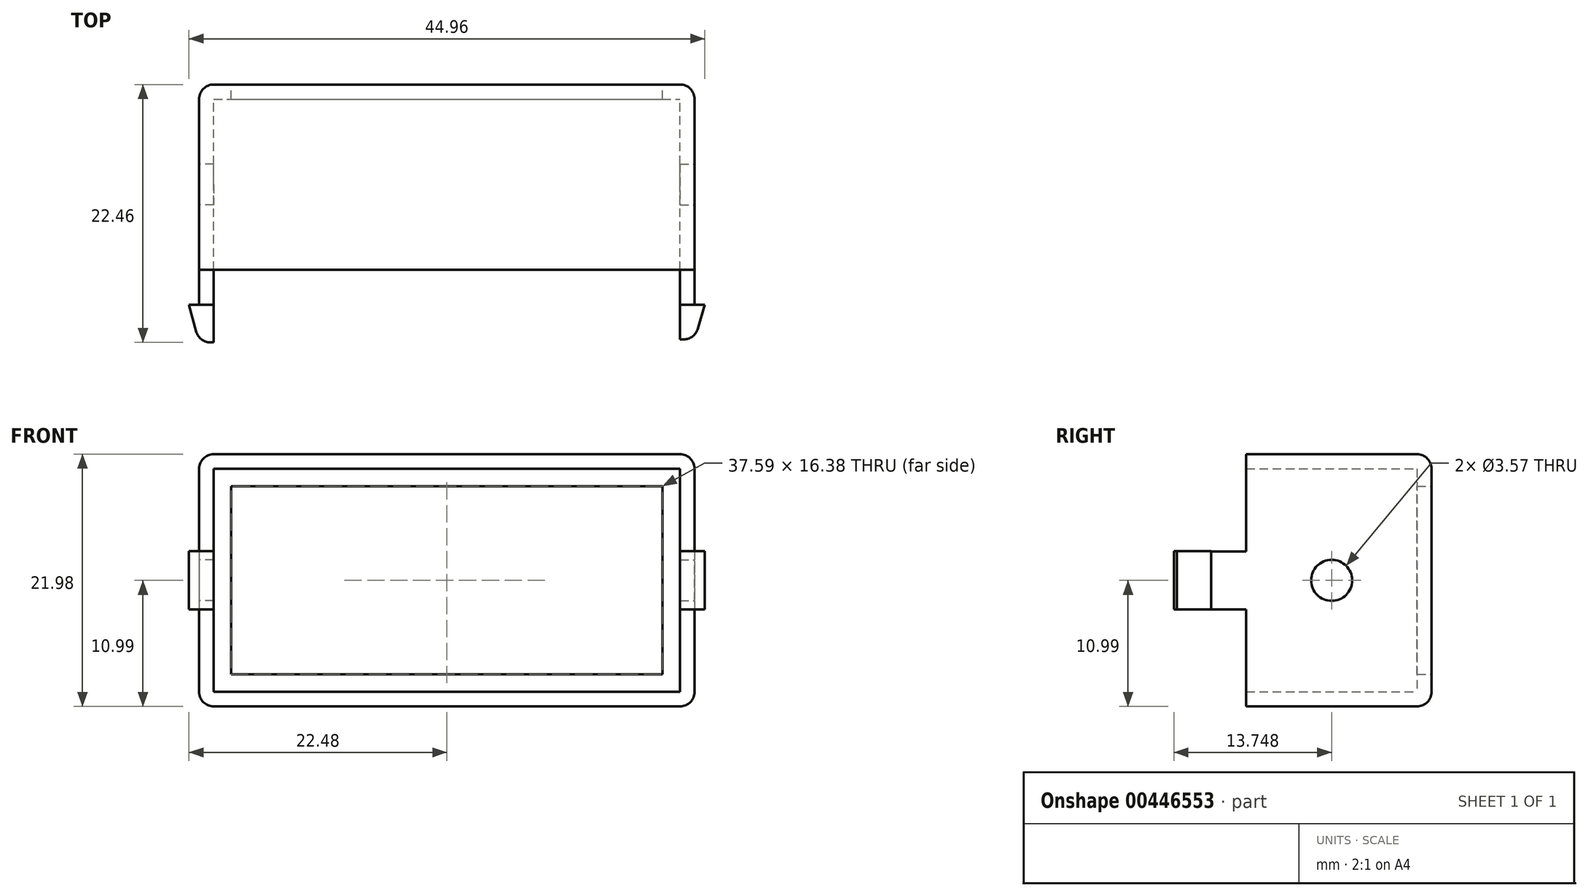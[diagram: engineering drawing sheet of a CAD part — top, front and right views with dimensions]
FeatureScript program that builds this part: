
annotation { "Feature Type Name" : "Feature", "Feature Type Description" : "" }
export const myFeature = defineFeature(function(context is Context, id is Id, definition is map)
    precondition{}
    {
        {
            var Q0;
            Q0=qCreatedBy(makeId("Front.planeOp"),FACE);
            var sketch = newSketch(context, id + "F0", { "sketchPlane" : qUnion([Q0])});
            skLineSegment(sketch, "E0.bottom", {"start": v(21.59, 10.99) * mm, "end": v(-21.59, 10.99) * mm});
            skLineSegment(sketch, "E0.top", {"start": v(21.59, -10.99) * mm, "end": v(-21.59, -10.99) * mm});
            skLineSegment(sketch, "E0.left", {"start": v(21.59, 10.99) * mm, "end": v(21.59, -10.99) * mm});
            skLineSegment(sketch, "E0.right", {"start": v(-21.59, 10.99) * mm, "end": v(-21.59, -10.99) * mm});
            skPoint(sketch, "E0.middle", {"position": v(0, 0) * mm});
            skLineSegment(sketch, "E1.bottom", {"start": v(-18.8, -8.2) * mm, "end": v(18.8, -8.2) * mm});
            skLineSegment(sketch, "E1.top", {"start": v(-18.8, 8.2) * mm, "end": v(18.8, 8.2) * mm});
            skLineSegment(sketch, "E1.left", {"start": v(-18.8, -8.2) * mm, "end": v(-18.8, 8.2) * mm});
            skLineSegment(sketch, "E1.right", {"start": v(18.8, -8.2) * mm, "end": v(18.8, 8.2) * mm});
            skLineSegment(sketch, "E2.bottom", {"start": v(-20.32, 9.72) * mm, "end": v(20.32, 9.72) * mm});
            skLineSegment(sketch, "E2.top", {"start": v(-20.32, -9.72) * mm, "end": v(20.32, -9.72) * mm});
            skLineSegment(sketch, "E2.left", {"start": v(-20.32, 9.72) * mm, "end": v(-20.32, -9.72) * mm});
            skLineSegment(sketch, "E2.right", {"start": v(20.32, 9.72) * mm, "end": v(20.32, -9.72) * mm});
            skSolve(sketch);
        }
        {
            var Q0;
            Q0=makeQuery(id+"F0.imprint","IMPRINT",FACE,{"disambiguationData":[TD([[makeQuery(id+"F0.imprint","IMPRINT",EDGE,{"derivedFrom":sQuery(id+"F0.wireOp",EDGE,"E0.bottom")}),1.0]])]});
            extrude(context, id + "F1", {"entities" : qUnion([Q0]), "depth" : 16.15 * mm});
        }
        {
            var Q0;
            Q0=makeQuery(id+"F0.imprint","IMPRINT",FACE,{"disambiguationData":[TD([[makeQuery(id+"F0.imprint","IMPRINT",EDGE,{"derivedFrom":sQuery(id+"F0.wireOp",EDGE,"E1.bottom")}),-1.0]])]});
            extrude(context, id + "F2", {"entities" : qUnion([Q0]), "operationType" : NewBodyOperationType.ADD, "depth" : 1.27 * mm});
        }
        {
            var Q0;
            Q0=makeQuery(id+"F1.opExtrude","SWEPT_EDGE",EDGE,{"disambiguationData":[OSD([sQuery(id+"F0.wireOp",EDGE,"E0.bottom"),sQuery(id+"F0.wireOp",EDGE,"E0.right")])]});
            var Q1;
            Q1=makeQuery(id+"F1.opExtrude","SWEPT_EDGE",EDGE,{"disambiguationData":[OSD([sQuery(id+"F0.wireOp",EDGE,"E0.top"),sQuery(id+"F0.wireOp",EDGE,"E0.right")])]});
            var Q2;
            Q2=makeQuery(id+"F1.opExtrude","SWEPT_EDGE",EDGE,{"disambiguationData":[OSD([sQuery(id+"F0.wireOp",EDGE,"E0.top"),sQuery(id+"F0.wireOp",EDGE,"E0.left")])]});
            var Q3;
            Q3=makeQuery(id+"F1.opExtrude","SWEPT_EDGE",EDGE,{"disambiguationData":[OSD([sQuery(id+"F0.wireOp",EDGE,"E0.bottom"),sQuery(id+"F0.wireOp",EDGE,"E0.left")])]});
            fillet(context, id + "F3", {"entities" : qUnion([Q0, Q1, Q2, Q3]), "radius" : 1.27 * mm, "tangentPropagation" : true, "allowEdgeOverflow" : false});
        }
        {
            var Q0;
            Q0=makeQuery(id+"F1.opExtrude","CAP_EDGE",EDGE,{"disambiguationData":[OSD([sQuery(id+"F0.wireOp",EDGE,"E0.top")])],"isStart":true});
            fillet(context, id + "F4", {"entities" : qUnion([Q0]), "radius" : 1.27 * mm, "tangentPropagation" : true, "allowEdgeOverflow" : false});
        }
        {
            var Q0;
            Q0=makeQuery(id+"F1.opExtrude","SWEPT_FACE",FACE,{"disambiguationData":[OSD([sQuery(id+"F0.wireOp",EDGE,"E0.left")])]});
            var sketch = newSketch(context, id + "F5", { "sketchPlane" : qUnion([Q0])});
            skLineSegment(sketch, "E3", {"start": v(-8.71, 9.72) * mm, "end": v(-8.71, -9.72) * mm, "construction": true});
            skLineSegment(sketch, "E4", {"start": v(-16.15, 0) * mm, "end": v(-1.27, 0) * mm, "construction": true});
            skCircle(sketch, "E5", {"center": v(-8.71, 0) * mm, "radius": 1.79 * mm});
            skSolve(sketch);
        }
        {
            var Q0;
            Q0=makeQuery(id+"F5.imprint","IMPRINT",FACE,{"disambiguationData":[TD([[makeQuery(id+"F5.imprint","IMPRINT",EDGE,{"derivedFrom":sQuery(id+"F5.wireOp",EDGE,"E5")}),1.0]])]});
            extrude(context, id + "F6", {"entities" : qUnion([Q0]), "operationType" : NewBodyOperationType.REMOVE, "oppositeDirection" : true, "depth" : 7.62 * mm});
        }
        {
            var Q0;
            Q0=makeQuery(id+"F1.opExtrude","SWEPT_FACE",FACE,{"disambiguationData":[OSD([sQuery(id+"F0.wireOp",EDGE,"E0.right")])]});
            var sketch = newSketch(context, id + "F7", { "sketchPlane" : qUnion([Q0])});
            skLineSegment(sketch, "E6", {"start": v(8.71, -9.72) * mm, "end": v(8.71, 9.72) * mm, "construction": true});
            skLineSegment(sketch, "E7", {"start": v(16.15, 0) * mm, "end": v(1.27, 0) * mm, "construction": true});
            skCircle(sketch, "E8", {"center": v(8.71, 0) * mm, "radius": 1.79 * mm});
            skSolve(sketch);
        }
        {
            var Q0;
            Q0=makeQuery(id+"F7.imprint","IMPRINT",FACE,{"disambiguationData":[TD([[makeQuery(id+"F7.imprint","IMPRINT",EDGE,{"derivedFrom":sQuery(id+"F7.wireOp",EDGE,"E8")}),1.0]])]});
            extrude(context, id + "F8", {"entities" : qUnion([Q0]), "operationType" : NewBodyOperationType.REMOVE, "oppositeDirection" : true, "depth" : 7.62 * mm});
        }
        {
            var Q0;
            Q0=makeQuery(id+"F1.opExtrude","CAP_FACE",FACE,{"disambiguationData":[OSD([sQuery(id+"F0.wireOp",EDGE,"E0.bottom"),sQuery(id+"F0.wireOp",EDGE,"E0.top"),sQuery(id+"F0.wireOp",EDGE,"E0.left"),sQuery(id+"F0.wireOp",EDGE,"E0.right"),sQuery(id+"F0.wireOp",EDGE,"E2.bottom"),sQuery(id+"F0.wireOp",EDGE,"E2.top"),sQuery(id+"F0.wireOp",EDGE,"E2.left"),sQuery(id+"F0.wireOp",EDGE,"E2.right")])],"isStart":false});
            var sketch = newSketch(context, id + "F9", { "sketchPlane" : qUnion([Q0])});
            skLineSegment(sketch, "E9.bottom", {"start": v(-21.59, 0) * mm, "end": v(-20.32, 0) * mm, "construction": true});
            skLineSegment(sketch, "E9.top", {"start": v(-21.59, 2.53) * mm, "end": v(-20.32, 2.53) * mm, "construction": true});
            skLineSegment(sketch, "E9.left", {"start": v(-21.59, 0) * mm, "end": v(-21.59, 2.53) * mm, "construction": true});
            skLineSegment(sketch, "E9.right", {"start": v(-20.32, 0) * mm, "end": v(-20.32, 2.53) * mm, "construction": true});
            skLineSegment(sketch, "E10.top", {"start": v(-21.59, -2.54) * mm, "end": v(-20.32, -2.54) * mm, "construction": true});
            skLineSegment(sketch, "E10.left", {"start": v(-21.59, 0) * mm, "end": v(-21.59, -2.54) * mm, "construction": true});
            skLineSegment(sketch, "E10.right", {"start": v(-20.32, 0) * mm, "end": v(-20.32, -2.54) * mm, "construction": true});
            skLineSegment(sketch, "E11.bottom", {"start": v(-21.59, -2.54) * mm, "end": v(-20.32, -2.54) * mm});
            skLineSegment(sketch, "E11.top", {"start": v(-21.59, 2.53) * mm, "end": v(-20.32, 2.53) * mm});
            skLineSegment(sketch, "E11.left", {"start": v(-21.59, -2.54) * mm, "end": v(-21.59, 2.53) * mm});
            skLineSegment(sketch, "E11.right", {"start": v(-20.32, -2.54) * mm, "end": v(-20.32, 2.53) * mm});
            skLineSegment(sketch, "E12.bottom", {"start": v(21.59, 0) * mm, "end": v(20.32, 0) * mm, "construction": true});
            skLineSegment(sketch, "E12.top", {"start": v(21.59, 2.53) * mm, "end": v(20.32, 2.53) * mm, "construction": true});
            skLineSegment(sketch, "E12.left", {"start": v(21.59, 0) * mm, "end": v(21.59, 2.53) * mm, "construction": true});
            skLineSegment(sketch, "E12.right", {"start": v(20.32, 0) * mm, "end": v(20.32, 2.53) * mm, "construction": true});
            skLineSegment(sketch, "E13.top", {"start": v(21.59, -2.54) * mm, "end": v(20.32, -2.54) * mm, "construction": true});
            skLineSegment(sketch, "E13.left", {"start": v(21.59, 0) * mm, "end": v(21.59, -2.54) * mm, "construction": true});
            skLineSegment(sketch, "E13.right", {"start": v(20.32, 0) * mm, "end": v(20.32, -2.54) * mm, "construction": true});
            skLineSegment(sketch, "E14.bottom", {"start": v(20.32, 2.53) * mm, "end": v(21.59, 2.53) * mm});
            skLineSegment(sketch, "E14.top", {"start": v(20.32, -2.54) * mm, "end": v(21.59, -2.54) * mm});
            skLineSegment(sketch, "E14.left", {"start": v(20.32, 2.53) * mm, "end": v(20.32, -2.54) * mm});
            skLineSegment(sketch, "E14.right", {"start": v(21.59, 2.53) * mm, "end": v(21.59, -2.54) * mm});
            skSolve(sketch);
        }
        {
            var Q0;
            Q0 = qSketchRegion(id + "F9", true);
            extrude(context, id + "F10", {"entities" : qUnion([Q0]), "operationType" : NewBodyOperationType.ADD, "depth" : 3.05 * mm});
        }
        {
            var Q0;
            Q0=makeQuery(id+"F10.opExtrude","SWEPT_FACE",FACE,{"disambiguationData":[OSD([sQuery(id+"F9.wireOp",EDGE,"E14.top")])]});
            var sketch = newSketch(context, id + "F11", { "sketchPlane" : qUnion([Q0])});
            skLineSegment(sketch, "E15", {"start": v(20.32, 19.2) * mm, "end": v(20.32, 22.2) * mm, "construction": true});
            skLineSegment(sketch, "E16", {"start": v(20.32, 22.2) * mm, "end": v(21.59, 22.2) * mm, "construction": true});
            skLineSegment(sketch, "E17", {"start": v(21.59, 22.2) * mm, "end": v(22.48, 19.2) * mm, "construction": true});
            skLineSegment(sketch, "E18", {"start": v(20.32, 19.2) * mm, "end": v(22.48, 19.2) * mm, "construction": true});
            skLineSegment(sketch, "E19", {"start": v(20.32, 19.2) * mm, "end": v(20.32, 22.2) * mm});
            skLineSegment(sketch, "E20", {"start": v(20.64, 22.2) * mm, "end": v(20.32, 22.2) * mm});
            skLineSegment(sketch, "E21", {"start": v(21.86, 21.3) * mm, "end": v(22.48, 19.2) * mm});
            skLineSegment(sketch, "E22", {"start": v(22.48, 19.2) * mm, "end": v(20.32, 19.2) * mm});
            skPoint(sketch, "E23.visualSharp", {"position": v(21.59, 22.2) * mm});
            skArc(sketch, "E23.filletArc", {"start": v(21.86, 21.3) * mm, "mid": v(21.4, 21.95) * mm, "end": v(20.64, 22.2) * mm});
            skSolve(sketch);
        }
        {
            var Q0;
            {var subQ4=sQuery(id+"F11.wireOp",EDGE,"E19");Q0=makeQuery(id+"F11.imprint","IMPRINT",FACE,{"disambiguationData":[TD([[makeQuery(id+"F11.imprint","IMPRINT",EDGE,{"derivedFrom":subQ4}),-1.0]])]});}
            extrude(context, id + "F12", {"entities" : qUnion([Q0]), "operationType" : NewBodyOperationType.ADD, "depth" : -5.08 * mm});
        }
        {
            var Q0;
            Q0=makeQuery(id+"F10.opExtrude","SWEPT_FACE",FACE,{"disambiguationData":[OSD([sQuery(id+"F9.wireOp",EDGE,"E11.bottom")])]});
            var sketch = newSketch(context, id + "F13", { "sketchPlane" : qUnion([Q0])});
            skLineSegment(sketch, "E24", {"start": v(-20.32, 19.2) * mm, "end": v(-20.32, 22.46) * mm, "construction": true});
            skLineSegment(sketch, "E25", {"start": v(-20.32, 22.46) * mm, "end": v(-21.58, 22.46) * mm, "construction": true});
            skLineSegment(sketch, "E26", {"start": v(-21.58, 22.46) * mm, "end": v(-22.48, 19.2) * mm, "construction": true});
            skLineSegment(sketch, "E27", {"start": v(-22.48, 19.2) * mm, "end": v(-20.32, 19.2) * mm, "construction": true});
            skLineSegment(sketch, "E28", {"start": v(-20.32, 19.2) * mm, "end": v(-20.32, 22.46) * mm});
            skLineSegment(sketch, "E29", {"start": v(-20.32, 22.46) * mm, "end": v(-20.61, 22.46) * mm});
            skLineSegment(sketch, "E30", {"start": v(-21.84, 21.53) * mm, "end": v(-22.48, 19.2) * mm});
            skLineSegment(sketch, "E31", {"start": v(-22.48, 19.2) * mm, "end": v(-20.32, 19.2) * mm});
            skPoint(sketch, "E32.visualSharp", {"position": v(-21.58, 22.46) * mm});
            skArc(sketch, "E32.filletArc", {"start": v(-20.61, 22.46) * mm, "mid": v(-21.38, 22.2) * mm, "end": v(-21.84, 21.53) * mm});
            skSolve(sketch);
        }
        {
            var Q0;
            {var subQ4=sQuery(id+"F13.wireOp",EDGE,"E28");Q0=makeQuery(id+"F13.imprint","IMPRINT",FACE,{"disambiguationData":[TD([[makeQuery(id+"F13.imprint","IMPRINT",EDGE,{"derivedFrom":subQ4}),1.0]])]});}
            extrude(context, id + "F14", {"entities" : qUnion([Q0]), "operationType" : NewBodyOperationType.ADD, "depth" : -5.08 * mm});
        }
    });
